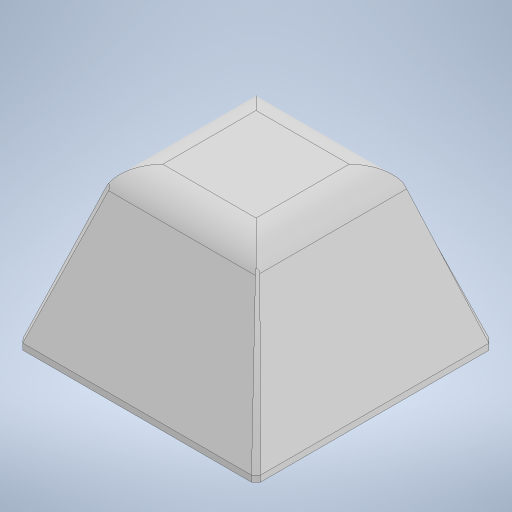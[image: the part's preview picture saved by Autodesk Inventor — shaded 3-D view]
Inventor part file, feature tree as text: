
AUTODESK INVENTOR PART (.ipt)
format: ipt  version: 2023 (Build 270158000, 158)  size: 279,040 bytes
history: native  units: in
note: dims shown in document units (in); Inventor stores cm internally (conversion verified against a paired STEP export)
features: sketch x2, extrude x1, plane x1, loft x1, fillet x1, other x1
ambient origin geometry x8: Origin, YZ Plane, XZ Plane, XY Plane, X Axis, Y Axis, Z Axis, Center Point
bodies: Solid1 (feature_tree)
feature tree (7):
  extrude  "Extrusion1"  Depth=0.1141in
  plane  "Work Plane1"
  sketch  "Sketch2"  dims[d2=5.8898in d3=5.8976in d4=5.8898in d5=5.8898in d6=0.116in d7=0.9274in d8=0.9477in d9=0.9277in d10=0.9276in d11=0.9279in d12=0.1575in d13=0.0in d14=3.937in d15=3.5433in d16=3.5433in d17=0.0in d18=90.0deg d19=0.0in d20=90.0deg d32=0.7874in]
  loft  "Loft1"
  fillet  "Fillet2"  Radius=5.8898in
  sketch  "Sketch1"  dims[d0=0.1141in d1=0.1141in]
  other  "Edges1"
